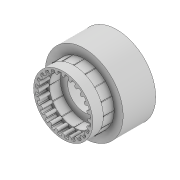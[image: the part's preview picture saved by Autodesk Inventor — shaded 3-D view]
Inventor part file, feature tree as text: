
AUTODESK INVENTOR PART (.ipt)
format: ipt  version: 2020 (Build 240168000, 168)  size: 548,352 bytes
history: native  units: in
note: dims shown in document units (in); Inventor stores cm internally (conversion verified against a paired STEP export)
features: extrude x5, sketch x5, chamfer x2
ambient origin geometry x8: Origin, YZ Plane, XZ Plane, XY Plane, X Axis, Y Axis, Z Axis, Center Point
bodies: Solid1 (feature_tree)
feature tree (12):
  extrude  "Extrusion1"  Depth=2.0472in
  extrude  "Extrusion2"  Depth=0.8563in
  chamfer  "Chamfer2"  Distance=0.2756in
  chamfer  "Chamfer3"  Distance=0.2756in
  extrude  "Extrusion3"  Depth=0.2756in
  extrude  "Extrusion4"  Depth=0.2756in TaperAngle=360.0deg
  extrude  "Extrusion5"  Depth=0.2756in TaperAngle=0.0deg
  sketch  "Sketch1"  dims[d0=0.8661in d1=2.0472in]
  sketch  "Sketch2"  dims[d2=0.8563in d3=0.0in d4=1.2598in]
  sketch  "Sketch3"  dims[d5=1.5748in d6=0.2756in d7=0.0in d11=0.2756in d12=0.125in d13=0.0137in]
  sketch  "Sketch4"  dims[d14=0.2756in d15=0.125in d16=0.0137in d17=0.0157in]
  sketch  "Sketch5"  dims[d18=0.0in d19=4.7244in d21=360.0deg d23=0.2756in d24=0.0in d25=0.0157in d26=6.2992in d28=360.0deg d30=0.2756in d31=0.0in d33=0.0394in d38=0.0394in d39=1.4567in d40=0.042in d41=0.042in d42=0.042in d43=9.4488in d45=360.0deg d47=0.2756in d48=0.0in]
